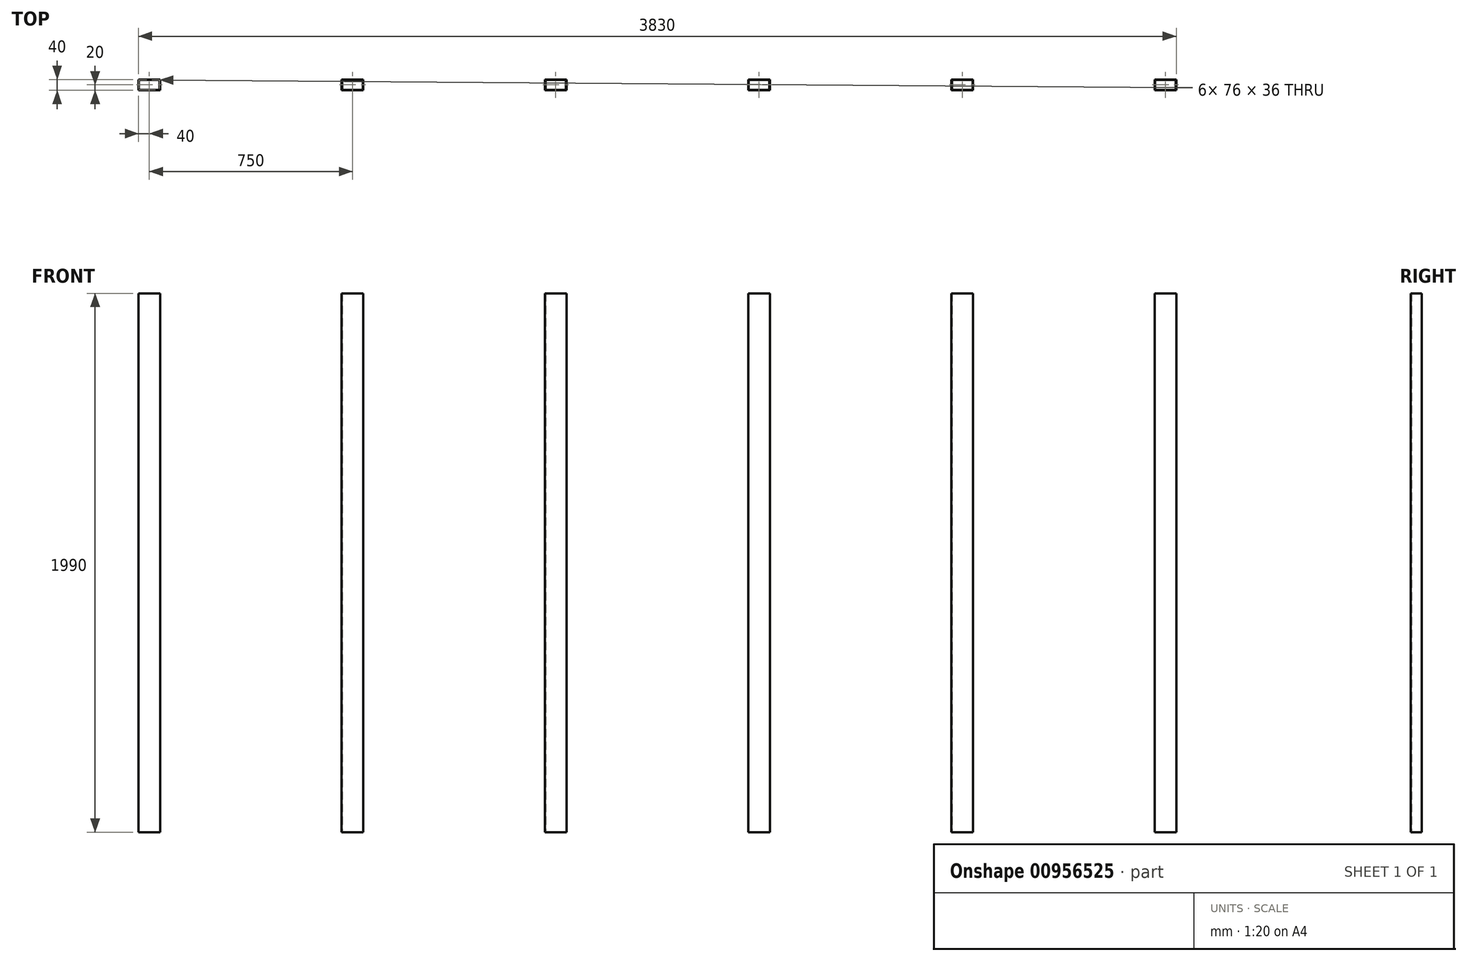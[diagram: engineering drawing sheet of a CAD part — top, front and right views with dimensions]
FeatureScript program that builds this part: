
annotation { "Feature Type Name" : "Feature", "Feature Type Description" : "" }
export const myFeature = defineFeature(function(context is Context, id is Id, definition is map)
    precondition{}
    {
        {
            var Q0;
            Q0=qCreatedBy(makeId("Top.planeOp"),FACE);
            var sketch = newSketch(context, id + "F0", { "sketchPlane" : qUnion([Q0])});
            skLineSegment(sketch, "E0.bottom", {"start": v(40, 20) * mm, "end": v(-40, 20) * mm});
            skLineSegment(sketch, "E0.top", {"start": v(40, -20) * mm, "end": v(-40, -20) * mm});
            skLineSegment(sketch, "E0.left", {"start": v(40, 20) * mm, "end": v(40, -20) * mm});
            skLineSegment(sketch, "E0.right", {"start": v(-40, 20) * mm, "end": v(-40, -20) * mm});
            skPoint(sketch, "E0.middle", {"position": v(0, 0) * mm});
            skLineSegment(sketch, "E1.0", {"start": v(38, 18) * mm, "end": v(-38, 18) * mm});
            skLineSegment(sketch, "E1.1", {"start": v(38, 18) * mm, "end": v(38, -18) * mm});
            skLineSegment(sketch, "E1.2", {"start": v(38, -18) * mm, "end": v(-38, -18) * mm});
            skLineSegment(sketch, "E1.3", {"start": v(-38, 18) * mm, "end": v(-38, -18) * mm});
            skPoint(sketch, "E2.1.0.0", {"position": v(750, 0) * mm});
            skLineSegment(sketch, "E2.1.0.1", {"start": v(788, -18) * mm, "end": v(712, -18) * mm});
            skLineSegment(sketch, "E2.1.0.2", {"start": v(788, 18) * mm, "end": v(712, 18) * mm});
            skLineSegment(sketch, "E2.1.0.3", {"start": v(790, 20) * mm, "end": v(710, 20) * mm});
            skLineSegment(sketch, "E2.1.0.4", {"start": v(712, 18) * mm, "end": v(712, -18) * mm});
            skLineSegment(sketch, "E2.1.0.5", {"start": v(788, 18) * mm, "end": v(788, -18) * mm});
            skLineSegment(sketch, "E2.1.0.6", {"start": v(710, 20) * mm, "end": v(710, -20) * mm});
            skLineSegment(sketch, "E2.1.0.7", {"start": v(790, 20) * mm, "end": v(790, -20) * mm});
            skLineSegment(sketch, "E2.1.0.8", {"start": v(790, -20) * mm, "end": v(710, -20) * mm});
            skPoint(sketch, "E2.2.0.0", {"position": v(1500, 0) * mm});
            skLineSegment(sketch, "E2.2.0.1", {"start": v(1538, -18) * mm, "end": v(1462, -18) * mm});
            skLineSegment(sketch, "E2.2.0.2", {"start": v(1538, 18) * mm, "end": v(1462, 18) * mm});
            skLineSegment(sketch, "E2.2.0.3", {"start": v(1540, 20) * mm, "end": v(1460, 20) * mm});
            skLineSegment(sketch, "E2.2.0.4", {"start": v(1462, 18) * mm, "end": v(1462, -18) * mm});
            skLineSegment(sketch, "E2.2.0.5", {"start": v(1538, 18) * mm, "end": v(1538, -18) * mm});
            skLineSegment(sketch, "E2.2.0.6", {"start": v(1460, 20) * mm, "end": v(1460, -20) * mm});
            skLineSegment(sketch, "E2.2.0.7", {"start": v(1540, 20) * mm, "end": v(1540, -20) * mm});
            skLineSegment(sketch, "E2.2.0.8", {"start": v(1540, -20) * mm, "end": v(1460, -20) * mm});
            skLineSegment(sketch, "E2.direction1", {"start": v(-40, -20) * mm, "end": v(710, -20) * mm, "construction": true});
            skPoint(sketch, "E3.0.3.0", {"position": v(2250, 0) * mm});
            skLineSegment(sketch, "E3.1.3.0", {"start": v(2288, -18) * mm, "end": v(2212, -18) * mm});
            skLineSegment(sketch, "E3.4.3.0", {"start": v(2288, 18) * mm, "end": v(2212, 18) * mm});
            skLineSegment(sketch, "E3.7.3.0", {"start": v(2290, 20) * mm, "end": v(2210, 20) * mm});
            skLineSegment(sketch, "E3.10.3.0", {"start": v(2212, 18) * mm, "end": v(2212, -18) * mm});
            skLineSegment(sketch, "E3.13.3.0", {"start": v(2288, 18) * mm, "end": v(2288, -18) * mm});
            skLineSegment(sketch, "E3.16.3.0", {"start": v(2210, 20) * mm, "end": v(2210, -20) * mm});
            skLineSegment(sketch, "E3.19.3.0", {"start": v(2290, 20) * mm, "end": v(2290, -20) * mm});
            skLineSegment(sketch, "E3.22.3.0", {"start": v(2290, -20) * mm, "end": v(2210, -20) * mm});
            skPoint(sketch, "E3.0.4.0", {"position": v(3000, 0) * mm});
            skLineSegment(sketch, "E3.1.4.0", {"start": v(3038, -18) * mm, "end": v(2962, -18) * mm});
            skLineSegment(sketch, "E3.4.4.0", {"start": v(3038, 18) * mm, "end": v(2962, 18) * mm});
            skLineSegment(sketch, "E3.7.4.0", {"start": v(3040, 20) * mm, "end": v(2960, 20) * mm});
            skLineSegment(sketch, "E3.10.4.0", {"start": v(2962, 18) * mm, "end": v(2962, -18) * mm});
            skLineSegment(sketch, "E3.13.4.0", {"start": v(3038, 18) * mm, "end": v(3038, -18) * mm});
            skLineSegment(sketch, "E3.16.4.0", {"start": v(2960, 20) * mm, "end": v(2960, -20) * mm});
            skLineSegment(sketch, "E3.19.4.0", {"start": v(3040, 20) * mm, "end": v(3040, -20) * mm});
            skLineSegment(sketch, "E3.22.4.0", {"start": v(3040, -20) * mm, "end": v(2960, -20) * mm});
            skPoint(sketch, "E3.0.5.0", {"position": v(3750, 0) * mm});
            skLineSegment(sketch, "E3.1.5.0", {"start": v(3788, -18) * mm, "end": v(3712, -18) * mm});
            skLineSegment(sketch, "E3.4.5.0", {"start": v(3788, 18) * mm, "end": v(3712, 18) * mm});
            skLineSegment(sketch, "E3.7.5.0", {"start": v(3790, 20) * mm, "end": v(3710, 20) * mm});
            skLineSegment(sketch, "E3.10.5.0", {"start": v(3712, 18) * mm, "end": v(3712, -18) * mm});
            skLineSegment(sketch, "E3.13.5.0", {"start": v(3788, 18) * mm, "end": v(3788, -18) * mm});
            skLineSegment(sketch, "E3.16.5.0", {"start": v(3710, 20) * mm, "end": v(3710, -20) * mm});
            skLineSegment(sketch, "E3.19.5.0", {"start": v(3790, 20) * mm, "end": v(3790, -20) * mm});
            skLineSegment(sketch, "E3.22.5.0", {"start": v(3790, -20) * mm, "end": v(3710, -20) * mm});
            skSolve(sketch);
        }
        {
            var Q0;
            Q0 = qSketchRegion(id + "F0", true);
            extrude(context, id + "F1", {"entities" : qUnion([Q0]), "depth" : 1990 * mm, "offsetDistance" : 25 * mm});
        }
    });
